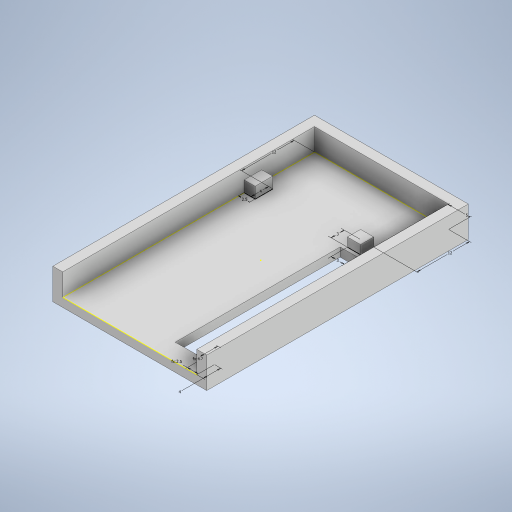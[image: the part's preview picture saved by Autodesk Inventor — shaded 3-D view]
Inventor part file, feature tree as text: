
AUTODESK INVENTOR PART (.ipt)
format: ipt  version: 2024 (Build 280153000, 153)  size: 295,936 bytes
history: native  units: in
note: dims shown in document units (in); Inventor stores cm internally (conversion verified against a paired STEP export)
features: extrude x5, sketch x4
ambient origin geometry x8: Origin, YZ Plane, XZ Plane, XY Plane, X Axis, Y Axis, Z Axis, Center Point
bodies: Solid1 (feature_tree)
feature tree (9):
  extrude  "Extrusion1"  Depth=1.378in
  extrude  "Extrusion2"  Depth=0.0886in
  sketch  "Sketch3"  dims[d5=0.0886in d6=0.0886in]
  extrude  "Extrusion3"  Depth=0.0886in
  extrude  "Extrusion4"  Depth=0.1181in
  extrude  "Extrusion5"  Depth=0.1181in
  sketch  "Sketch1"  dims[d0=2.3425in d1=1.378in]
  sketch  "Sketch2"  dims[d2=0.2756in d3=0.0in d4=0.0886in]
  sketch  "Sketch4"  dims[d7=0.1969in d8=0.0in d9=0.1181in d10=0.1181in d19=0.0787in d20=0.0in d21=0.4724in d22=0.1969in d23=0.0984in d24=0.1575in d25=0.1575in d26=0.0984in d27=0.4724in d28=0.1575in d29=0.0984in d30=0.0in d31=0.0984in d32=0.0in]
